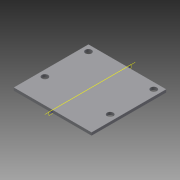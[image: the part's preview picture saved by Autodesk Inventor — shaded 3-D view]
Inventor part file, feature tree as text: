
AUTODESK INVENTOR PART (.ipt)
format: ipt  version: 2014 (Build 180170000, 170)  size: 88,576 bytes
history: native  units: mm
features: extrude x1, plane x1, sketch x1, other x1
ambient origin geometry x8: Origin, YZ Plane, XZ Plane, XY Plane, X Axis, Y Axis, Z Axis, Center Point
bodies: Volumenkörper1 (feature_tree)
feature tree (4):
  extrude  "Extrusion1"  Depth=24.0mm
  plane  "Arbeitsebene1"
  sketch  "Skizze1"  dims[d0=25.0mm d1=24.0mm d2=2.0mm d3=2.0mm d4=2.0mm d5=2.0mm d6=2.0mm d7=2.0mm d8=2.0mm d9=2.0mm d10=2.0mm d11=2.0mm d12=8.0mm d13=8.0mm d14=0.9mm d15=0.0mm d16=90.0deg]
  other  "Arbeitsachse1"
